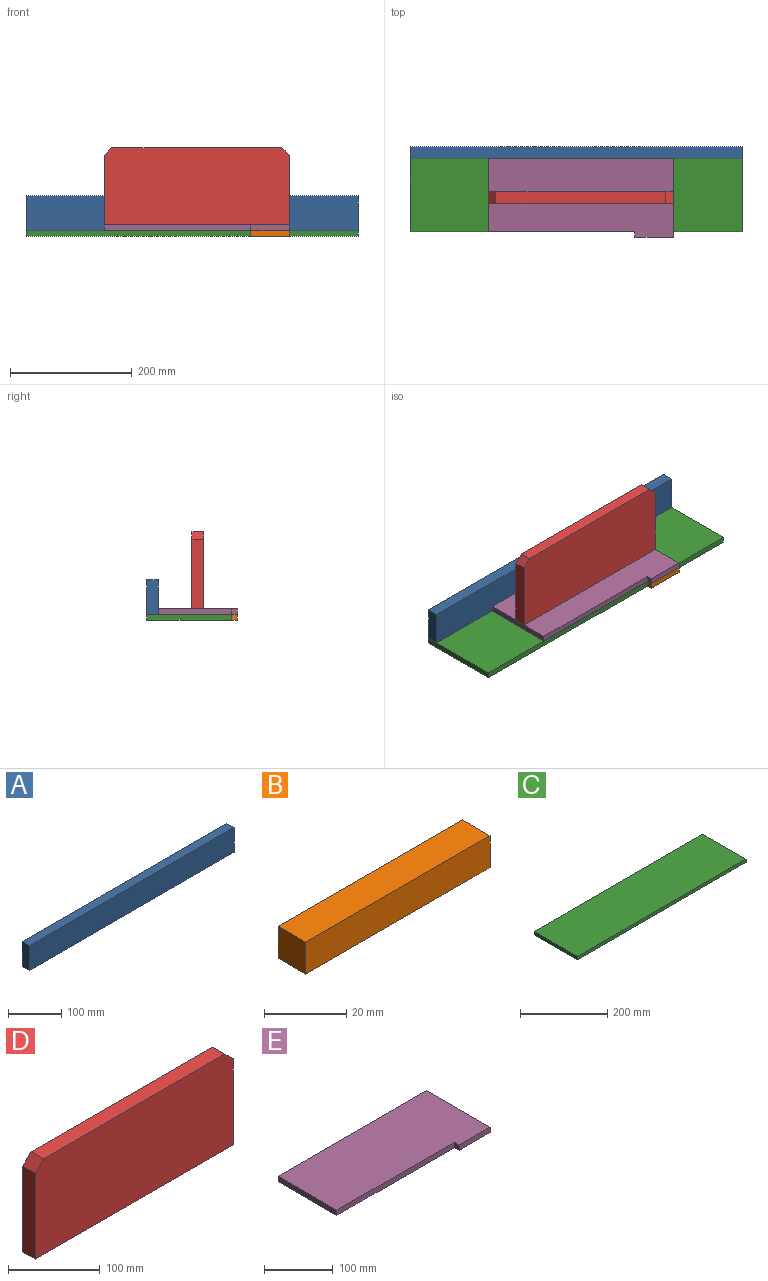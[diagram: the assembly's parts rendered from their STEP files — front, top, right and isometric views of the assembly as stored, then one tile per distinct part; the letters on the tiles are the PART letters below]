
ASSEMBLY  parts=5 mates=4
PART A: 6 faces, bbox 546.1x19.1x57.2 mm
  f0: plane 57.15x19.05mm, normal (-1,0,0), area 1088.7mm2, adj f1,f3,f4,f5
  f1: plane 546.1x57.15mm, normal (0,-1,0), area 31209.6mm2, adj f0,f2,f4,f5
  f2: plane 57.15x19.05mm, normal (1,0,0), area 1088.7mm2, adj f1,f3,f4,f5
  f3: plane 546.1x57.15mm, normal (0,1,0), area 31209.6mm2, adj f0,f2,f4,f5
  f4: plane 546.1x19.05mm, normal (0,0,1), area 10403.2mm2, adj f0,f1,f2,f3
  f5: plane 546.1x19.05mm, normal (0,0,-1), area 10403.2mm2, adj f0,f1,f2,f3
PART B: 6 faces, bbox 63.5x9.5x9.5 mm
  f0: plane 9.53x9.53mm, normal (-1,0,0), area 90.7mm2, adj f1,f3,f4,f5
  f1: plane 63.5x9.53mm, normal (0,1,0), area 604.8mm2, adj f0,f2,f4,f5
  f2: plane 9.53x9.53mm, normal (1,0,0), area 90.7mm2, adj f1,f3,f4,f5
  f3: plane 63.5x9.53mm, normal (0,-1,0), area 604.8mm2, adj f0,f2,f4,f5
  f4: plane 63.5x9.53mm, normal (0,0,-1), area 604.8mm2, adj f0,f1,f2,f3
  f5: plane 63.5x9.53mm, normal (0,0,1), area 604.8mm2, adj f0,f1,f2,f3
PART C: 6 faces, bbox 546.1x139.7x9.5 mm
  f0: plane 546.1x9.53mm, normal (0,1,0), area 5201.6mm2, adj f1,f3,f4,f5
  f1: plane 139.7x9.53mm, normal (-1,0,0), area 1330.6mm2, adj f0,f2,f4,f5
  f2: plane 546.1x9.53mm, normal (0,-1,0), area 5201.6mm2, adj f1,f3,f4,f5
  f3: plane 139.7x9.53mm, normal (1,0,0), area 1330.6mm2, adj f0,f2,f4,f5
  f4: plane 546.1x139.7mm, normal (0,0,1), area 76290.2mm2, adj f0,f1,f2,f3
  f5: plane 546.1x139.7mm, normal (0,0,-1), area 76290.2mm2, adj f0,f1,f2,f3
PART D: 8 faces, bbox 304.8x19.1x127 mm
  f0: plane 114.3x19.05mm, normal (-1,0,0), area 2177.4mm2, adj f1,f3,f5,f7
  f1: plane 304.8x127mm, normal (0,-1,0), area 38548.3mm2, adj f0,f2,f4,f5,f6,f7
  f2: plane 114.3x19.05mm, normal (1,0,0), area 2177.4mm2, adj f1,f3,f5,f6
  f3: plane 304.8x127mm, normal (0,1,0), area 38548.3mm2, adj f0,f2,f4,f5,f6,f7
  f4: plane 279.4x19.05mm, normal (0,0,1), area 5322.6mm2, adj f1,f3,f6,f7
  f5: plane 304.8x19.05mm, normal (0,0,-1), area 5806.4mm2, adj f0,f1,f2,f3
  f6: plane 19.05x12.7mm, normal (0.71,0,0.71), area 342.1mm2, adj f1,f2,f3,f4
  f7: plane 19.05x12.7mm, normal (-0.71,0,0.71), area 342.1mm2, adj f0,f1,f3,f4
PART E: 8 faces, bbox 304.8x130.2x9.5 mm
  f0: plane 130.18x9.53mm, normal (1,0,0), area 1239.9mm2, adj f1,f5,f6,f7
  f1: plane 304.8x9.53mm, normal (0,1,0), area 2903.2mm2, adj f0,f2,f6,f7
  f2: plane 120.65x9.53mm, normal (-1,0,0), area 1149.2mm2, adj f1,f3,f6,f7
  f3: plane 241.3x9.53mm, normal (0,-1,0), area 2298.4mm2, adj f2,f4,f6,f7
  f4: plane 9.53x9.53mm, normal (-1,0,0), area 90.7mm2, adj f3,f5,f6,f7
  f5: plane 63.5x9.53mm, normal (0,-1,0), area 604.8mm2, adj f0,f4,f6,f7
  f6: plane 304.8x130.18mm, normal (0,0,1), area 37379mm2, adj f0,f1,f2,f3,f4,f5
  f7: plane 304.8x130.18mm, normal (0,0,-1), area 37379mm2, adj f0,f1,f2,f3,f4,f5
PLACE A t=(120.6,215.22,-33.4)mm
PLACE B t=(100.89,0,-23.88)mm
PLACE C t=(120.6,215.22,-33.4)mm fixed
PLACE D t=(100.89,2.55,-23.88)mm
PLACE E t=(100.89,0,-23.88)mm
MATE slider E.f0 <-> A.f2  axis (1,0,0) through (162.73,103.74,-23.88)mm
MATE fastened D.f5 <-> E.f6  axis (0,0,-1) through (162.73,29.12,-14.35)mm
MATE fastened E.f7 <-> B.f5  axis (0,0,-1) through (162.73,-26.44,-23.88)mm
MATE fastened A.f5 <-> C.f4  axis (0,0,-1) through (275.53,122.79,-23.88)mm
